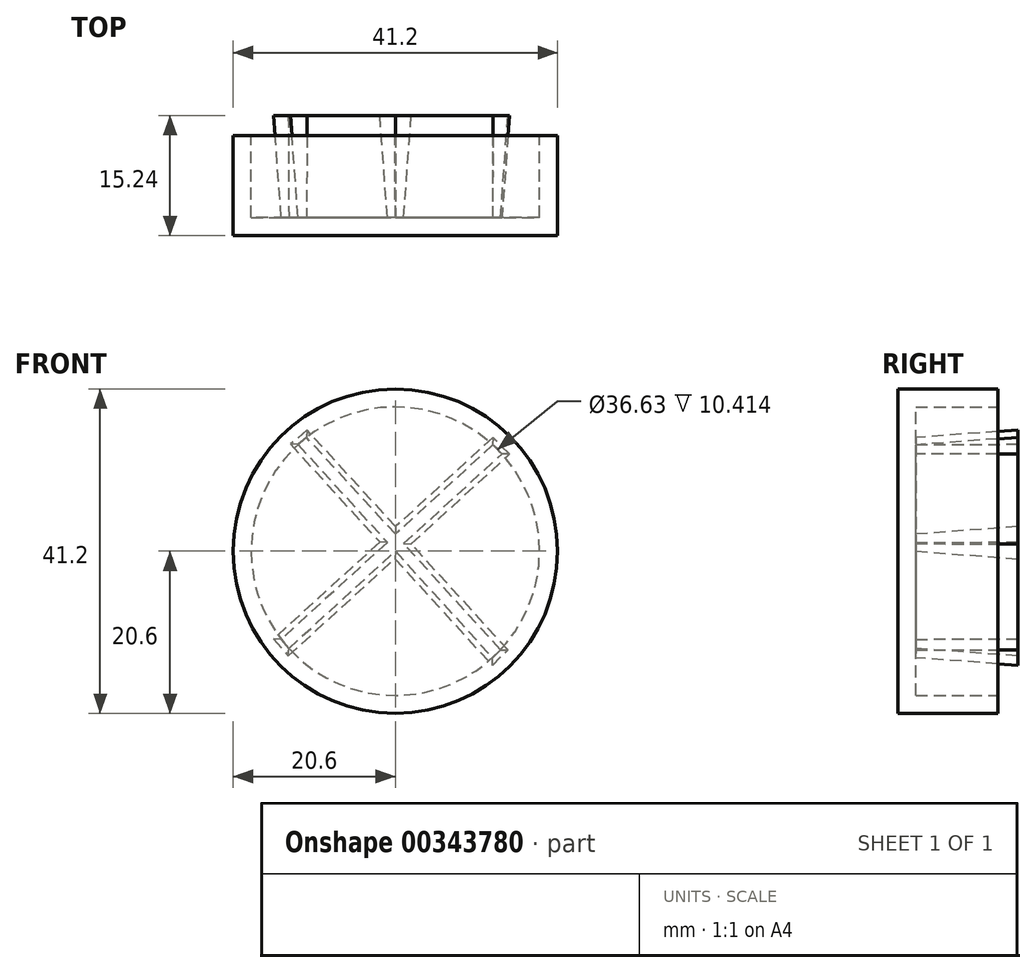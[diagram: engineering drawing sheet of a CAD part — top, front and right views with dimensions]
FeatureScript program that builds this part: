
annotation { "Feature Type Name" : "Feature", "Feature Type Description" : "" }
export const myFeature = defineFeature(function(context is Context, id is Id, definition is map)
    precondition{}
    {
        {
            var Q0;
            Q0=qCreatedBy(makeId("Front.planeOp"),FACE);
            var sketch = newSketch(context, id + "F0", { "sketchPlane" : qUnion([Q0])});
            skCircle(sketch, "E0", {"center": v(0, 0) * mm, "radius": 20.6 * mm});
            skSolve(sketch);
        }
        {
            var Q0;
            Q0=makeQuery(id+"F0.imprint","IMPRINT",FACE,{"disambiguationData":[TD([[makeQuery(id+"F0.imprint","IMPRINT",EDGE,{"derivedFrom":sQuery(id+"F0.wireOp",EDGE,"E0")}),1.0]])]});
            extrude(context, id + "F1", {"entities" : qUnion([Q0]), "depth" : 12.7 * mm});
        }
        {
            var Q0;
            Q0=makeQuery(id+"F1.opExtrude","CAP_FACE",FACE,{"disambiguationData":[OSD([sQuery(id+"F0.wireOp",EDGE,"E0")])],"isStart":true});
            shell(context, id + "F2", {"entities" : qUnion([Q0]), "thickness" : 2.3 * mm});
        }
        {
            var Q0;
            {var subQ0=sQuery(id+"F0.wireOp",EDGE,"E0");Q0=makeQuery(id+"F2.opShell","OFFSET_FACE",FACE,{"disambiguationData":[OSD([subQ0]),TDD([makeQuery(id+"F1.opExtrude","CAP_FACE",FACE,{"disambiguationData":[OSD([subQ0])],"isStart":false})])]});}
            var sketch = newSketch(context, id + "F3", { "sketchPlane" : qUnion([Q0])});
            skLineSegment(sketch, "E1", {"start": v(0, 0) * mm, "end": v(13.53, -12.34) * mm});
            skLineSegment(sketch, "E2", {"start": v(0, 0) * mm, "end": v(-12.34, -13.53) * mm});
            skLineSegment(sketch, "E3", {"start": v(1.01, 1.11) * mm, "end": v(12.34, 13.53) * mm});
            skLineSegment(sketch, "E4", {"start": v(-1.05, 0.96) * mm, "end": v(-13.05, 11.9) * mm});
            skLineSegment(sketch, "E5", {"start": v(-13.05, 11.9) * mm, "end": v(-13.53, 12.34) * mm});
            skLineSegment(sketch, "E6", {"start": v(-12.37, 13.51) * mm, "end": v(0, 2.16) * mm});
            skLineSegment(sketch, "E7", {"start": v(0, 2.16) * mm, "end": v(11.27, 14.44) * mm});
            skLineSegment(sketch, "E8", {"start": v(1.01, 1.11) * mm, "end": v(14.5, -11.2) * mm});
            skLineSegment(sketch, "E9", {"start": v(-1.05, 0.96) * mm, "end": v(-13.36, -12.53) * mm});
            skLineSegment(sketch, "E10", {"start": v(-13.53, 12.34) * mm, "end": v(-12.37, 13.51) * mm});
            skLineSegment(sketch, "E11", {"start": v(11.27, 14.44) * mm, "end": v(12.34, 13.53) * mm});
            skLineSegment(sketch, "E12", {"start": v(13.53, -12.34) * mm, "end": v(14.5, -11.2) * mm});
            skLineSegment(sketch, "E13", {"start": v(-12.34, -13.53) * mm, "end": v(-13.36, -12.53) * mm});
            skSolve(sketch);
        }
        {
            var Q0;
            Q0=makeQuery(id+"F3.imprint","IMPRINT",FACE,{"disambiguationData":[TD([[makeQuery(id+"F3.imprint","IMPRINT",EDGE,{"derivedFrom":sQuery(id+"F3.wireOp",EDGE,"E1")}),1.0]])]});
            extrude(context, id + "F4", {"entities" : qUnion([Q0]), "depth" : 12.95 * mm, "hasDraft" : true, "draftAngle" : 3 * degree});
        }
    });
